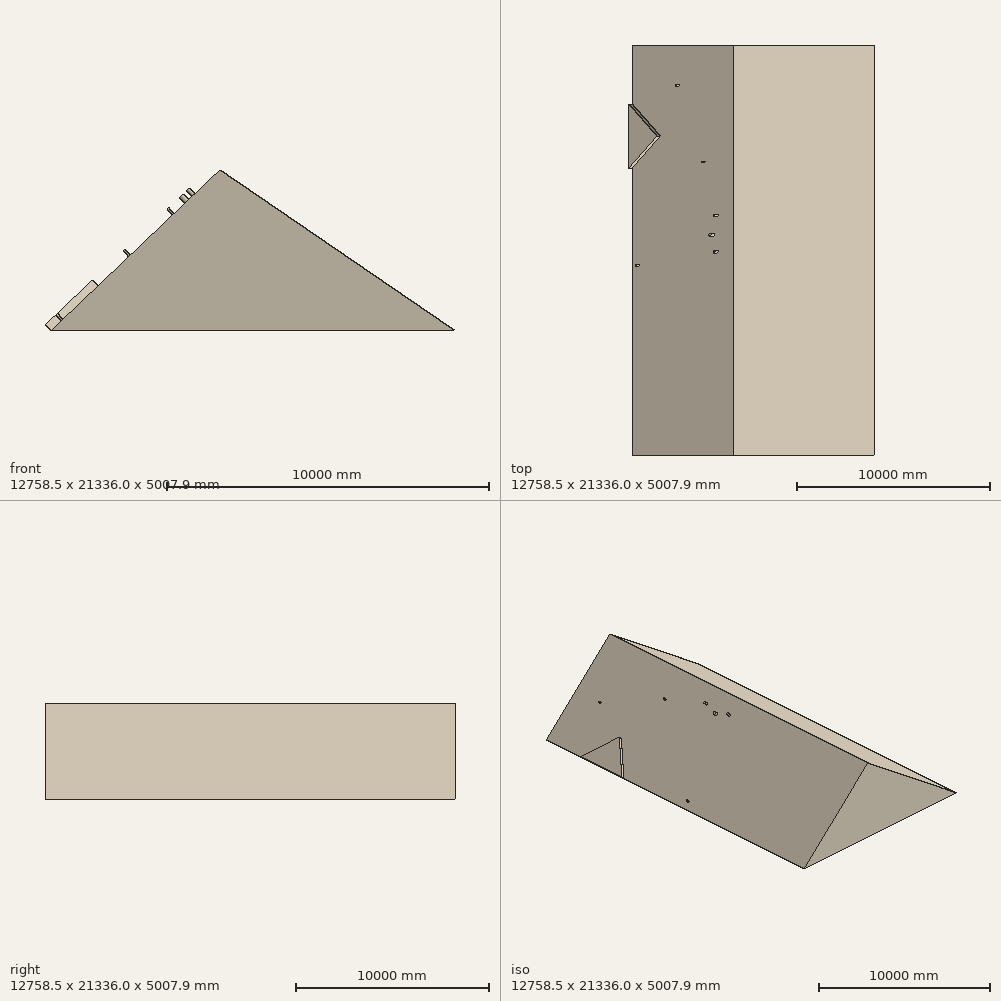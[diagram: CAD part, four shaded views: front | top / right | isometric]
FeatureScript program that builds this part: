
annotation { "Feature Type Name" : "Feature", "Feature Type Description" : "" }
export const myFeature = defineFeature(function(context is Context, id is Id, definition is map)
    precondition{}
    {
        {
            var Q0;
            Q0=qCreatedBy(makeId("Front.planeOp"),FACE);
            var sketch = newSketch(context, id + "F0", { "sketchPlane" : qUnion([Q0])});
            skLineSegment(sketch, "E0", {"start": v(-5262.35, 0) * mm, "end": v(7321.03, 0) * mm});
            skLineSegment(sketch, "E1", {"start": v(7321.03, 0) * mm, "end": v(0, 5007.9) * mm});
            skLineSegment(sketch, "E2", {"start": v(0, 5007.9) * mm, "end": v(-5262.35, 0) * mm});
            skSolve(sketch);
        }
        {
            var Q0;
            Q0 = qSketchRegion(id + "F0", true);
            extrude(context, id + "F1", {"entities" : qUnion([Q0]), "depth" : 21336 * mm, "offsetDistance" : 25.4 * mm});
        }
        {
            var Q0;
            Q0=makeQuery(id+"F1.opExtrude","SWEPT_FACE",FACE,{"disambiguationData":[OSD([sQuery(id+"F0.wireOp",EDGE,"E2")])]});
            var sketch = newSketch(context, id + "F2", { "sketchPlane" : qUnion([Q0])});
            skCircle(sketch, "E3", {"center": v(-433.86, -2082.8) * mm, "radius": 38.1 * mm});
            skSolve(sketch);
        }
        {
            var Q0;
            Q0 = qSketchRegion(id + "F2", true);
            extrude(context, id + "F3", {"entities" : qUnion([Q0]), "operationType" : NewBodyOperationType.ADD, "depth" : 254 * mm, "offsetDistance" : 25.4 * mm});
        }
        {
            var Q0;
            Q0=makeQuery(id+"F1.opExtrude","SWEPT_FACE",FACE,{"disambiguationData":[OSD([sQuery(id+"F0.wireOp",EDGE,"E2")])]});
            var sketch = newSketch(context, id + "F4", { "sketchPlane" : qUnion([Q0])});
            skCircle(sketch, "E4", {"center": v(-3329.46, -11455.4) * mm, "radius": 38.1 * mm});
            skSolve(sketch);
        }
        {
            var Q0;
            Q0 = qSketchRegion(id + "F4", true);
            extrude(context, id + "F5", {"entities" : qUnion([Q0]), "operationType" : NewBodyOperationType.ADD, "depth" : 254 * mm, "offsetDistance" : 25.4 * mm});
        }
        {
            var Q0;
            Q0=makeQuery(id+"F1.opExtrude","SWEPT_FACE",FACE,{"disambiguationData":[OSD([sQuery(id+"F0.wireOp",EDGE,"E2")])]});
            var sketch = newSketch(context, id + "F6", { "sketchPlane" : qUnion([Q0])});
            skCircle(sketch, "E5", {"center": v(1445.74, -6070.6) * mm, "radius": 38.1 * mm});
            skSolve(sketch);
        }
        {
            var Q0;
            Q0 = qSketchRegion(id + "F6", true);
            extrude(context, id + "F7", {"entities" : qUnion([Q0]), "operationType" : NewBodyOperationType.ADD, "depth" : 254 * mm, "offsetDistance" : 25.4 * mm});
        }
        {
            var Q0;
            Q0=makeQuery(id+"F1.opExtrude","SWEPT_FACE",FACE,{"disambiguationData":[OSD([sQuery(id+"F0.wireOp",EDGE,"E2")])]});
            var sketch = newSketch(context, id + "F8", { "sketchPlane" : qUnion([Q0])});
            skCircle(sketch, "E6", {"center": v(2309.34, -8839.2) * mm, "radius": 63.5 * mm});
            skSolve(sketch);
        }
        {
            var Q0;
            Q0 = qSketchRegion(id + "F8", true);
            extrude(context, id + "F9", {"entities" : qUnion([Q0]), "operationType" : NewBodyOperationType.ADD, "depth" : 254 * mm, "offsetDistance" : 25.4 * mm});
        }
        {
            var Q0;
            Q0=makeQuery(id+"F1.opExtrude","SWEPT_FACE",FACE,{"disambiguationData":[OSD([sQuery(id+"F0.wireOp",EDGE,"E2")])]});
            var sketch = newSketch(context, id + "F10", { "sketchPlane" : qUnion([Q0])});
            skCircle(sketch, "E7", {"center": v(2309.34, -10744.2) * mm, "radius": 63.5 * mm});
            skSolve(sketch);
        }
        {
            var Q0;
            Q0 = qSketchRegion(id + "F10", true);
            extrude(context, id + "F11", {"entities" : qUnion([Q0]), "operationType" : NewBodyOperationType.ADD, "depth" : 254 * mm, "offsetDistance" : 25.4 * mm});
        }
        {
            var Q0;
            Q0=makeQuery(id+"F1.opExtrude","SWEPT_FACE",FACE,{"disambiguationData":[OSD([sQuery(id+"F0.wireOp",EDGE,"E2")])]});
            var sketch = newSketch(context, id + "F12", { "sketchPlane" : qUnion([Q0])});
            skCircle(sketch, "E8", {"center": v(2017.24, -9855.2) * mm, "radius": 88.9 * mm});
            skSolve(sketch);
        }
        {
            var Q0;
            Q0 = qSketchRegion(id + "F12", true);
            extrude(context, id + "F13", {"entities" : qUnion([Q0]), "operationType" : NewBodyOperationType.ADD, "depth" : 254 * mm, "offsetDistance" : 25.4 * mm});
        }
        {
            var Q0;
            Q0=makeQuery(id+"F1.opExtrude","SWEPT_FACE",FACE,{"disambiguationData":[OSD([sQuery(id+"F0.wireOp",EDGE,"E2")])]});
            var sketch = newSketch(context, id + "F14", { "sketchPlane" : qUnion([Q0])});
            skLineSegment(sketch, "E9", {"start": v(-3812.06, -3048) * mm, "end": v(-3812.06, -6400.8) * mm});
            skLineSegment(sketch, "E10", {"start": v(-3812.06, -6400.8) * mm, "end": v(-1780.06, -4724.4) * mm});
            skLineSegment(sketch, "E11", {"start": v(-1780.06, -4724.4) * mm, "end": v(-3812.06, -3048) * mm});
            skSolve(sketch);
        }
        {
            var Q0;
            Q0 = qSketchRegion(id + "F14", true);
            extrude(context, id + "F15", {"entities" : qUnion([Q0]), "operationType" : NewBodyOperationType.ADD, "depth" : 254 * mm, "offsetDistance" : 25.4 * mm});
        }
    });
